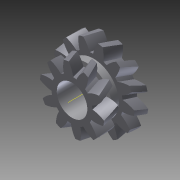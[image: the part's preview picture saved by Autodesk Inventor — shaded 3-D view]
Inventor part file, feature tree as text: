
AUTODESK INVENTOR PART (.ipt)
format: ipt  version: 2012 (Build 160160000, 160)  size: 572,928 bytes
history: native  units: in
note: dims shown in document units (in); Inventor stores cm internally (conversion verified against a paired STEP export)
features: other x5, extrude x3, sketch x3, projected_geometry x1
ambient origin geometry x8: Origin, YZ Plane, XZ Plane, XY Plane, X Axis, Y Axis, Z Axis, Center Point
bodies: Solid2 (feature_tree)
feature tree (12):
  other  "LargeSmallTransferGear.iam"
  other  "BlankGearLargeAndSmall.ipt:1"
  other  "Spur Gear1:1"
  other  "Spur Gear2:1"
  extrude  "Extrusion3"  Depth=0.3937in TaperAngle=0.0deg
  extrude  "Extrusion4"  Depth=0.3346in
  extrude  "Extrusion5"  [1 undecoded]
  other  "Work Axis2"
  sketch  "Sketch4"  dims[d5=0.3937in d6=0.3937in d7=0.0in]
  projected_geometry  "Projected Loop2"
  sketch  "Sketch5"  dims[d8=0.3937in d9=0.0in d10=0.3346in]
  sketch  "Sketch6"  dims[d12=0.3937in d13=0.0in]
note: 1 required parameter value undecoded (feature->parameter linkage not recoverable at this tier; creation-order binding heuristic only, values carry confidence <= 0.55)
